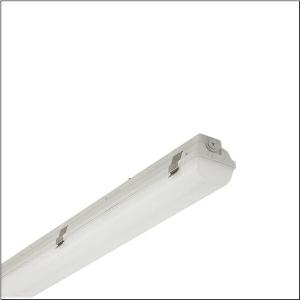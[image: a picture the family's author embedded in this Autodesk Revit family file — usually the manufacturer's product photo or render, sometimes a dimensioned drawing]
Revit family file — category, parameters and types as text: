
# Revit family: monsun_r__21_eco_51fj20dl45a_bcca
name_source: partatom
category: Lighting Fixtures
units: mm (PartAtom-declared; Revit-internal decimal feet)

## family parameters
Cut with Voids When Loaded = No
Host = Face
Light Source = No
Part Type = Normal
Room Calculation Point = No
Round Connector Dimension = Use Diameter
Shared = No

## types (1)
- Monsun® 21 Eco (1 x LED, 4900 lm, 36 W, 4000K)
    Apparent Load = 36 VA
    CIE Flux Codes = 40 69 88 88 100
    Color Rendering = 80
    Color Temperature = 4000K
    Default Elevation = 1800 mm
    Description = Monsun® 21 Eco, damp-proof luminaire, primary optical cover: diffuser, of PC, UV-stabilised, frosted, light emission: direct distribution, primary light characteristic: symmetric, installation type: suspended mounting, surface-mounted, LED, rated luminous flux: 4.900lm, luminous efficacy: 132lm/W, light colour: 840, colour temperature: 4000K, control gear: ECG DALI, with terminal, 5-pole, max. 2.5mm², mains connection: 220..240V, AC, 50/60Hz, rated input power: 36W, housing, of glass-fibre reinforced polyester, light grey (RAL 7035), length: 1.277mm, width: 90mm, height: 95mm, clip for enclosure, of spring steel V2A, protection rating (complete): IP66, insulation class (complete): insulation class I (protective earthing), certification: CE, UKCA, protection symbol: D, impact resistance: IK08, permissible operating ambient temperature: -20..+35°C, corresponds to IFS (International Featured Standards) requirements for safety and quality in the food industry, contact your sales advisor before using the luminaires in applications with unclear chemical exposure, large temperature fluctuations or condensation-forming humidity, packaging unit: 1 piece
    Height = 103 mm
    Lamp = 1 x LED
    Lamp Light Flux = 4900 lm
    Lamp Power = 36 W
    Lamp count = 1
    Length = 1277 mm
    Luminous efficacy = 136 lm/W
    Manufacturer = Siteco
    ModVariant = No
    Model = 51FJ20DL45A
    Mounting Place = Ceiling
    Mounting Type = Surface mounted
    Number of Poles = 1
    OnlyDefault = Yes
    Power Factor = 1
    Product Name = Monsun® 21 Eco
    Product group = damp-proof luminaire
    ProductGroupID = 301
    Protection Class = Protection class I
    Protection Degree = IP 66
    RLX_Detail_Level = 1
    RLX_Emergency_Light_Flux = 0 lm
    RLX_Emergency_Type = 0
    RLX_Emergency_Type_DB = No
    RlxData = <blob elided: 33405 chars, md5=6d087f97>
    Socket = socket
    Standby Power = 0 W
    System Light Flux = 4900 lm
    System Power = 36 W
    Type Comments = Product without accessories
    Type Image = l_1007218.jpg
    URL = http://relux.com
    VarID = ---
    Voltage = 0 V
    Weight = 0.00 kg
    Width = 90 mm

## geometry (parser evidence)
native form markers: Blend x4, Sweep x15
no freeform markers — native parametric forms only
